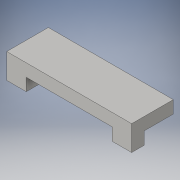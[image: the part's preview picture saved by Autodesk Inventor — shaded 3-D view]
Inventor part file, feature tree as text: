
AUTODESK INVENTOR PART (.ipt)
format: ipt  version: 2016 (Build 200138000, 138)  size: 111,104 bytes
history: native  units: mm
features: extrude x2, sketch x2, other x1
ambient origin geometry x8: Origin, YZ Plane, XZ Plane, XY Plane, X Axis, Y Axis, Z Axis, Center Point
bodies: Solid1 (feature_tree)
feature tree (5):
  other  "<userpath>\Documents\GitHub\3D\Hoja Oculta\Parametros.xlsx"
  extrude  "Cuerpo"  Depth=10.0mm
  extrude  "Agarres"  Depth=4.7mm
  sketch  "Sketch1"  dims[d0=30.0mm d1=10.0mm]
  sketch  "Sketch2"  dims[d2=3.0mm d3=0.0mm d4=4.7mm d5=3.0mm d6=3.0mm d7=4.7mm d8=3.0mm d9=0.0mm]
